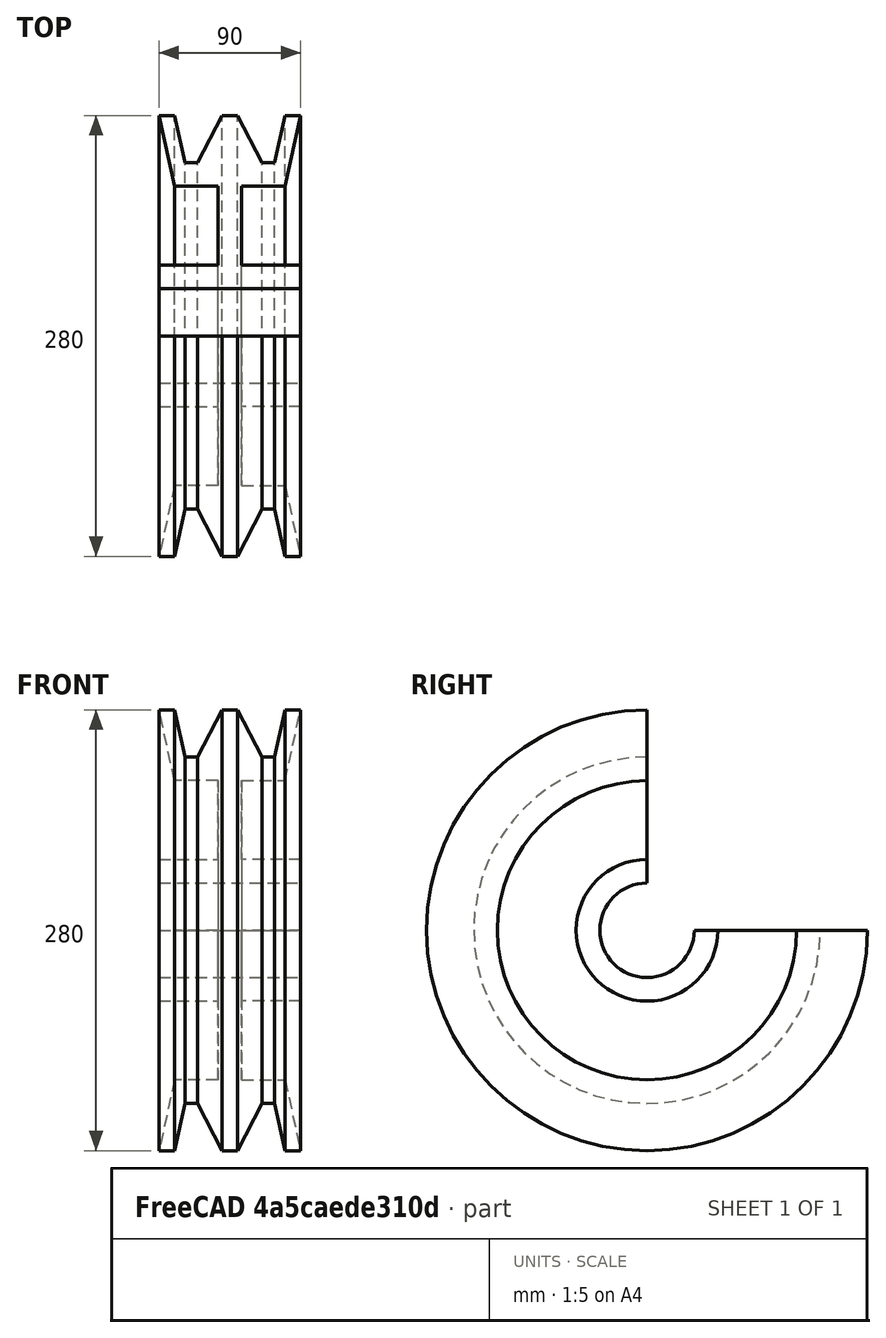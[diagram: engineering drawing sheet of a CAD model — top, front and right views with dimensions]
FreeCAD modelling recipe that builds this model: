
FCSTD DOCUMENT  (FreeCAD 0.16R)
Label: Ejer Final 30
License: All rights reserved
LicenseURL: http://en.wikipedia.org/wiki/All_rights_reserved
objects: Sketcher::SketchObject×1, PartDesign::Revolution×1
note: 3 computed .brp shape members not serialized (recipe doc carries the construction recipe); baked Part::Feature solids carry a one-line shape summary decoded from their .brp

FEATURE [Sketcher::SketchObject] Sketch
  Placement = pos=(0,0,0) rot=(-1,0,0;4.71239rad)
  sketch-geometry (22):
    g0: LineSegment StartX=-45 StartY=30 StartZ=0 EndX=45 EndY=30 EndZ=0
    g1: LineSegment StartX=-45 StartY=30 StartZ=0 EndX=-45 EndY=45 EndZ=0
    g2: LineSegment StartX=45 StartY=30 StartZ=0 EndX=45 EndY=45 EndZ=0
    g3: LineSegment StartX=-45 StartY=45 StartZ=0 EndX=-7.5 EndY=45 EndZ=0
    g4: LineSegment StartX=45 StartY=45 StartZ=0 EndX=7.5 EndY=45 EndZ=0
    g5: LineSegment StartX=7.5 StartY=45 StartZ=0 EndX=7.5 EndY=95 EndZ=0
    g6: LineSegment StartX=-7.5 StartY=45 StartZ=0 EndX=-7.5 EndY=95 EndZ=0
    g7: LineSegment StartX=7.5 StartY=95 StartZ=0 EndX=35 EndY=95 EndZ=0
    g8: LineSegment StartX=-7.5 StartY=95 StartZ=0 EndX=-35 EndY=95 EndZ=0
    g9: LineSegment StartX=-35 StartY=95 StartZ=0 EndX=-45 EndY=140 EndZ=0
    g10: LineSegment StartX=35 StartY=95 StartZ=0 EndX=45 EndY=140 EndZ=0
    g11: LineSegment [constr] StartX=35 StartY=95 StartZ=0 EndX=74.7048 EndY=95 EndZ=0
    g12: LineSegment [constr] StartX=-35 StartY=95 StartZ=0 EndX=-62.7601 EndY=95 EndZ=0
    g13: LineSegment StartX=-45 StartY=140 StartZ=0 EndX=-35 EndY=140 EndZ=0
    g14: LineSegment StartX=-35 StartY=140 StartZ=0 EndX=-28.3333 EndY=110 EndZ=0
    g15: LineSegment StartX=-28.3333 StartY=110 StartZ=0 EndX=-20.5978 EndY=110 EndZ=0
    g16: LineSegment StartX=-20.5978 StartY=110 StartZ=0 EndX=-5 EndY=140 EndZ=0
    g17: LineSegment StartX=-5 StartY=140 StartZ=0 EndX=5 EndY=140 EndZ=0
    g18: LineSegment StartX=5 StartY=140 StartZ=0 EndX=20.5978 EndY=110 EndZ=0
    g19: LineSegment StartX=20.5978 StartY=110 StartZ=0 EndX=28.3333 EndY=110 EndZ=0
    g20: LineSegment StartX=28.3333 StartY=110 StartZ=0 EndX=35 EndY=140 EndZ=0
    g21: LineSegment StartX=35 StartY=140 StartZ=0 EndX=45 EndY=140 EndZ=0
  constraints (62):
    c: Horizontal(g0)
    c: DistanceY(g-1,g0) = 30
    c: DistanceX(g0,g0) = 90
    c: Symmetric(g0,g0,g-2)
    c: Coincident(g1,g0)
    c: Vertical(g1)
    c: Coincident(g2,g0)
    c: Vertical(g2)
    c: DistanceY(g1,g1) = 15
    c: Horizontal(g3)
    c: Horizontal(g4)
    c: Symmetric(g3,g4,g-2)
    c: DistanceX(g3,g4) = 15
    c: Coincident(g5,g4)
    c: Vertical(g5)
    c: Coincident(g6,g3)
    c: Vertical(g6)
    c: DistanceY(g-1,g5) = 95
    c: Equal(g6,g5)
    c: Coincident(g7,g5)
    c: Horizontal(g7)
    c: Coincident(g8,g6)
    c: Horizontal(g8)
    c: Coincident(g9,g8)
    c: Coincident(g10,g7)
    c: Coincident(g11,g7)
    c: Horizontal(g11)
    c: Coincident(g12,g8)
    c: Horizontal(g12)
    c: DistanceX(g9,g10) = 90
    c: Coincident(g13,g9)
    c: Horizontal(g13)
    c: Coincident(g14,g13)
    c: Coincident(g15,g14)
    c: Coincident(g16,g17)
    c: Coincident(g17,g18)
    c: Coincident(g18,g19)
    c: Horizontal(g19)
    c: Coincident(g19,g20)
    c: Coincident(g20,g21)
    c: Coincident(g21,g10)
    c: Horizontal(g21)
    c: DistanceX(g13,g16) = 30
    c: DistanceX(g17,g20) = 30
    c: DistanceX(g17,g17) = 10
    c: Symmetric(g17,g16,g-2)
    c: DistanceX(g21,g21) = 10
    c: Angle(g16,g14) = 0.698132
    c: Coincident(g16,g15)
    c: Horizontal(g15)
    c: Angle(g20,g18) = 0.698132
    c: DistanceY(g14,g13) = 30
    c: DistanceY(g15,g16) = 30
    c: DistanceY(g19,g20) = 30
    c: Parallel(g14,g9)
    c: Parallel(g20,g10)
    c: DistanceY(g-1,g10) = 140
    c: DistanceY(g-1,g17) = 140
    c: DistanceX(g8,g7) = 70
    c: Symmetric(g7,g8,g-2)
    c: Coincident(g1,g3)
    c: Coincident(g2,g4)
FEATURE [PartDesign::Revolution] Revolution
  Angle = 270
  Axis = (1,0,0)
  Base = (0,0,0)
  Placement = pos=(0,0,0) rot=(-1,0,0;4.71239rad)
  ReferenceAxis = -> Sketch [H_Axis]
  Sketch = -> Sketch
